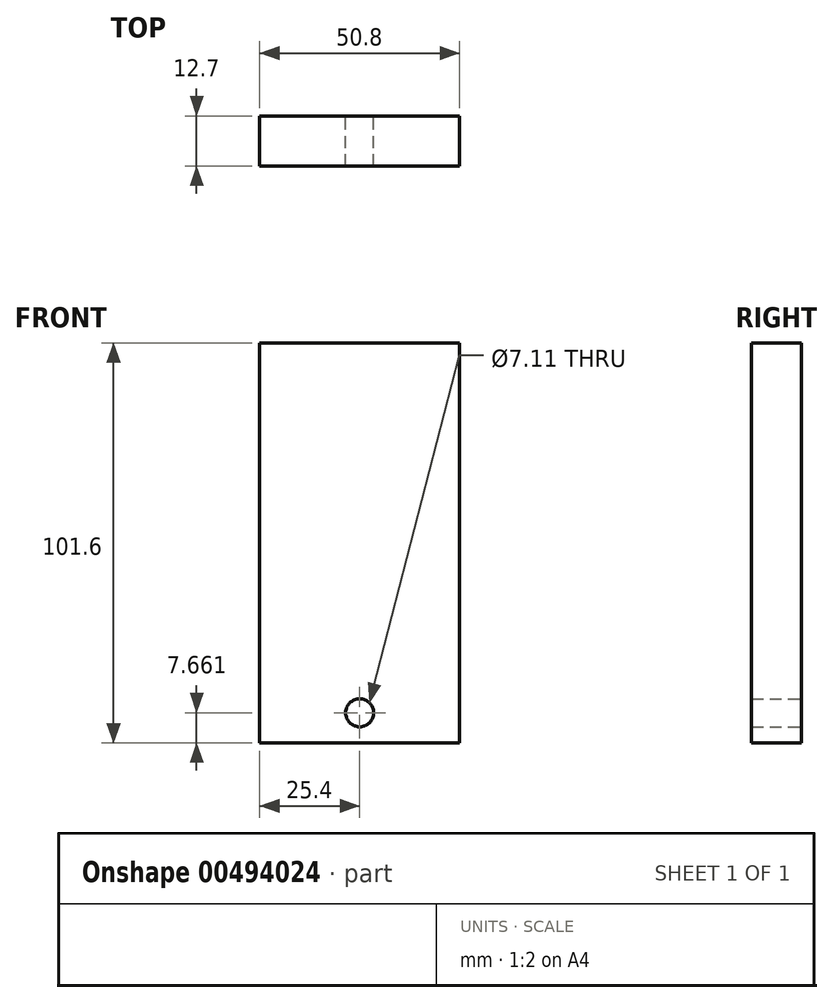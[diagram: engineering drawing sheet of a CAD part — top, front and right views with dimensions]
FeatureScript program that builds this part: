
annotation { "Feature Type Name" : "Feature", "Feature Type Description" : "" }
export const myFeature = defineFeature(function(context is Context, id is Id, definition is map)
    precondition{}
    {
        {
            var Q0;
            Q0=qCreatedBy(makeId("Front.planeOp"),FACE);
            var sketch = newSketch(context, id + "F0", { "sketchPlane" : qUnion([Q0])});
            skLineSegment(sketch, "E0.bottom", {"start": v(25.4, -50.8) * mm, "end": v(-25.4, -50.8) * mm});
            skLineSegment(sketch, "E0.top", {"start": v(25.4, 50.8) * mm, "end": v(-25.4, 50.8) * mm});
            skLineSegment(sketch, "E0.left", {"start": v(25.4, -50.8) * mm, "end": v(25.4, 50.8) * mm});
            skLineSegment(sketch, "E0.right", {"start": v(-25.4, -50.8) * mm, "end": v(-25.4, 50.8) * mm});
            skPoint(sketch, "E0.middle", {"position": v(0, 0) * mm});
            skCircle(sketch, "E1", {"center": v(0, -43.14) * mm, "radius": 3.55 * mm});
            skSolve(sketch);
        }
        {
            var Q0;
            Q0 = qSketchRegion(id + "F0", true);
            extrude(context, id + "F1", {"entities" : qUnion([Q0]), "depth" : 12.7 * mm});
        }
    });
